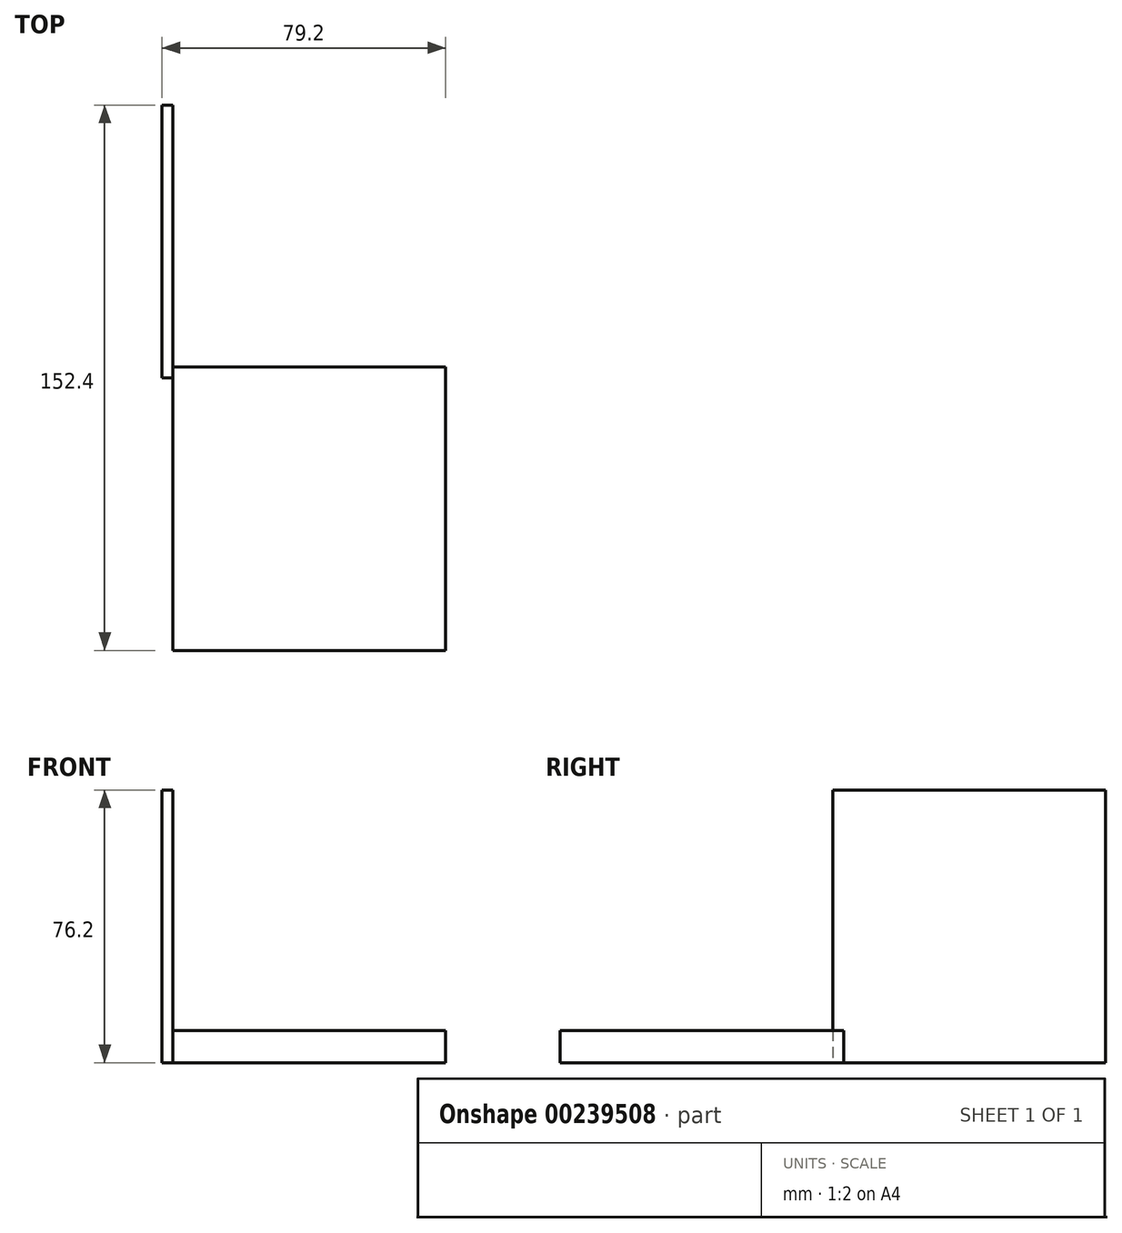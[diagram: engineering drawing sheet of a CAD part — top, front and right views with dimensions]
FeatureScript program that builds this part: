
annotation { "Feature Type Name" : "Feature", "Feature Type Description" : "" }
export const myFeature = defineFeature(function(context is Context, id is Id, definition is map)
    precondition{}
    {
        {
            assignVariable(context, id + "F0", {"name" : "L", "anyValue" : 3});
        }
        {
            var Q0;
            Q0=qCreatedBy(makeId("Top.planeOp"),FACE);
            var sketch = newSketch(context, id + "F1", { "sketchPlane" : qUnion([Q0])});
            skLineSegment(sketch, "E0.bottom", {"start": v(38.1, -38.1) * mm, "end": v(-38.1, -38.1) * mm});
            skLineSegment(sketch, "E0.top", {"start": v(38.1, 38.1) * mm, "end": v(-38.1, 38.1) * mm});
            skLineSegment(sketch, "E0.left", {"start": v(38.1, -38.1) * mm, "end": v(38.1, 38.1) * mm});
            skLineSegment(sketch, "E0.right", {"start": v(-38.1, -38.1) * mm, "end": v(-38.1, 38.1) * mm});
            skPoint(sketch, "E0.middle", {"position": v(0, 0) * mm});
            skSolve(sketch);
        }
        {
            var Q0;
            Q0 = qSketchRegion(id + "F1", true);
            extrude(context, id + "F2", {"entities" : qUnion([Q0]), "depth" : (getVariable(context, 'L') * (3)) * mm});
        }
        {
            var Q0;
            Q0=makeQuery(id+"F2.opExtrude","SWEPT_FACE",FACE,{"disambiguationData":[OSD([sQuery(id+"F1.wireOp",EDGE,"E0.top")])]});
            var sketch = newSketch(context, id + "F3", { "sketchPlane" : qUnion([Q0])});
            skLineSegment(sketch, "E1.bottom", {"start": v(38.1, 0) * mm, "end": v(-38.1, 0) * mm});
            skLineSegment(sketch, "E1.top", {"start": v(38.1, 76.2) * mm, "end": v(-38.1, 76.2) * mm});
            skLineSegment(sketch, "E1.left", {"start": v(38.1, 0) * mm, "end": v(38.1, 76.2) * mm});
            skLineSegment(sketch, "E1.right", {"start": v(-38.1, 0) * mm, "end": v(-38.1, 76.2) * mm});
            skSolve(sketch);
        }
        {
            var Q0;
            Q0=makeQuery(id+"F3.imprint","IMPRINT",FACE,{"disambiguationData":[TD([[makeQuery(id+"F3.imprint","IMPRINT",EDGE,{"derivedFrom":sQuery(id+"F3.wireOp",EDGE,"E1.bottom")}),1.0]])]});
            extrude(context, id + "F4", {"entities" : qUnion([Q0]), "operationType" : NewBodyOperationType.ADD, "depth" : (getVariable(context, 'L')) * mm});
        }
        {
            var Q0;
            Q0=makeQuery(id+"F4.boolean.opBoolean","MERGE",FACE,{"derivedFrom":[makeQuery(id+"F2.opExtrude","SWEPT_FACE",FACE,{"disambiguationData":[OSD([sQuery(id+"F1.wireOp",EDGE,"E0.right")])]}),makeQuery(id+"F4.opExtrude","SWEPT_FACE",FACE,{"disambiguationData":[OSD([sQuery(id+"F3.wireOp",EDGE,"E1.left")])]})]});
            var sketch = newSketch(context, id + "F5", { "sketchPlane" : qUnion([Q0])});
            skLineSegment(sketch, "E2.bottom", {"start": v(-114.3, 76.2) * mm, "end": v(-38.1, 76.2) * mm});
            skLineSegment(sketch, "E2.top", {"start": v(-114.3, 0) * mm, "end": v(-38.1, 0) * mm});
            skLineSegment(sketch, "E2.left", {"start": v(-114.3, 76.2) * mm, "end": v(-114.3, 0) * mm});
            skLineSegment(sketch, "E2.right", {"start": v(-38.1, 76.2) * mm, "end": v(-38.1, 0) * mm});
            skSolve(sketch);
        }
        {
            var Q0;
            Q0 = qSketchRegion(id + "F5", true);
            extrude(context, id + "F6", {"entities" : qUnion([Q0]), "operationType" : NewBodyOperationType.ADD, "depth" : (getVariable(context, 'L')) * mm});
        }
    });
